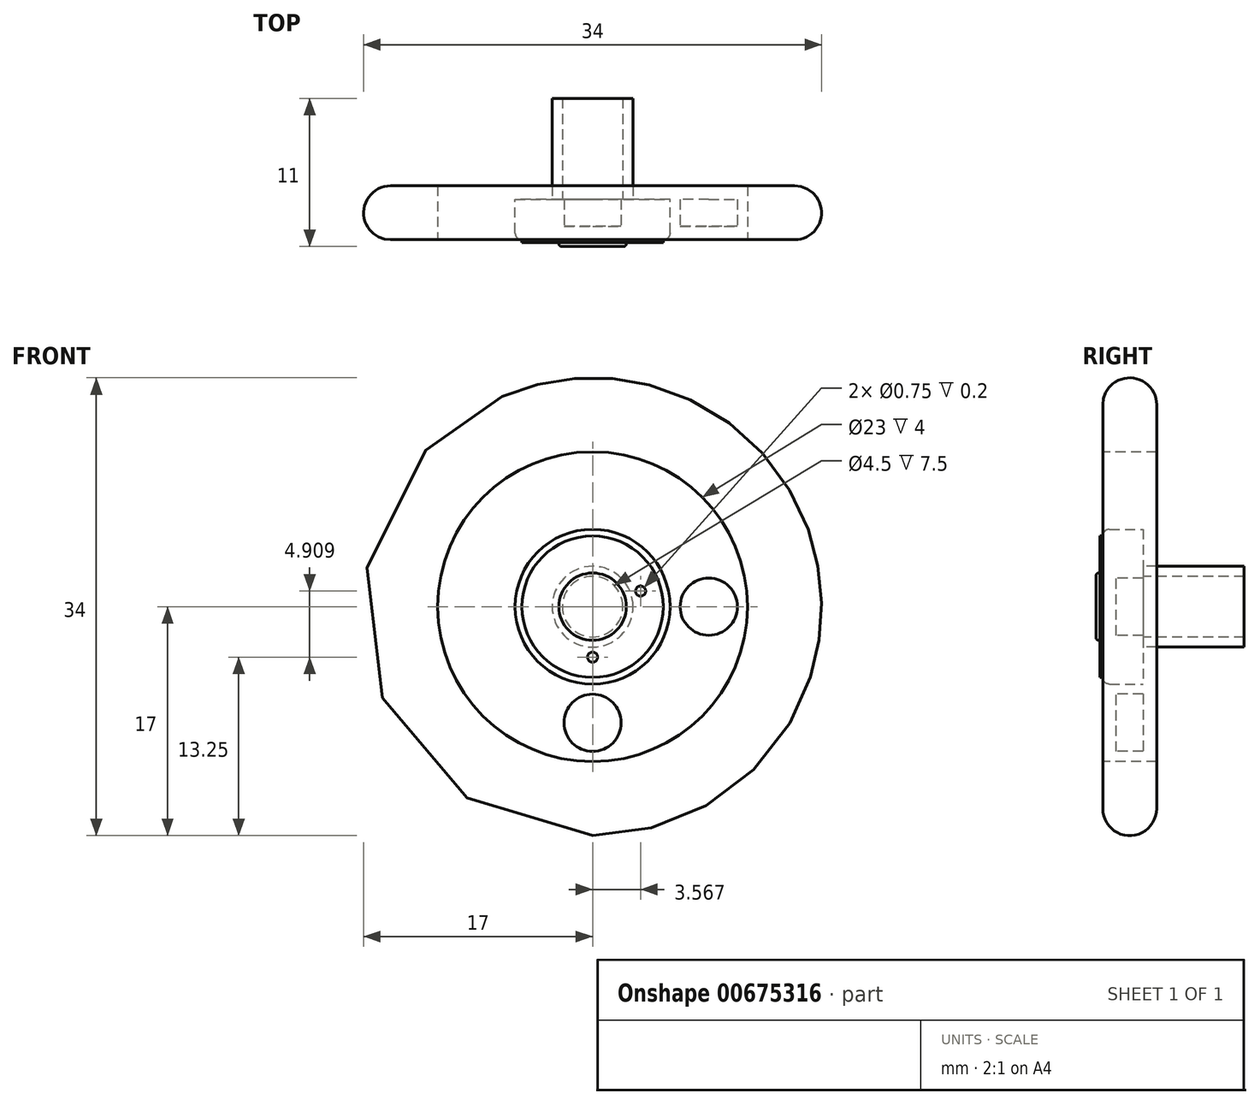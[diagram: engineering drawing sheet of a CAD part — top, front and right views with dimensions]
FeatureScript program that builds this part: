
annotation { "Feature Type Name" : "Feature", "Feature Type Description" : "" }
export const myFeature = defineFeature(function(context is Context, id is Id, definition is map)
    precondition{}
    {
        {
            var Q0;
            Q0=qCreatedBy(makeId("Front.planeOp"),FACE);
            var sketch = newSketch(context, id + "F0", { "sketchPlane" : qUnion([Q0])});
            skCircle(sketch, "E0", {"center": v(0, 0) * mm, "radius": 17 * mm});
            skSolve(sketch);
        }
        {
            var Q0;
            Q0 = qSketchRegion(id + "F0", true);
            extrude(context, id + "F1", {"entities" : qUnion([Q0]), "oppositeDirection" : true, "depth" : 4 * mm, "offsetDistance" : 25.4 * mm});
        }
        {
            var Q0;
            Q0=makeQuery(id+"F1.opExtrude","CAP_FACE",FACE,{"disambiguationData":[OSD([sQuery(id+"F0.wireOp",EDGE,"E0")])],"isStart":true});
            var sketch = newSketch(context, id + "F2", { "sketchPlane" : qUnion([Q0])});
            skCircle(sketch, "E1", {"center": v(0, 0) * mm, "radius": 11.5 * mm});
            skSolve(sketch);
        }
        {
            var Q0;
            Q0 = qSketchRegion(id + "F2", true);
            extrude(context, id + "F3", {"entities" : qUnion([Q0]), "operationType" : NewBodyOperationType.REMOVE, "oppositeDirection" : true, "depth" : 1 * mm, "offsetDistance" : 25.4 * mm});
        }
        {
            var Q0;
            Q0=makeQuery(id+"F1.opExtrude","CAP_FACE",FACE,{"disambiguationData":[OSD([sQuery(id+"F0.wireOp",EDGE,"E0")])],"isStart":false});
            var sketch = newSketch(context, id + "F4", { "sketchPlane" : qUnion([Q0])});
            skCircle(sketch, "E2", {"center": v(0, 0) * mm, "radius": 11.5 * mm});
            skSolve(sketch);
        }
        {
            var Q0;
            Q0 = qSketchRegion(id + "F4", true);
            extrude(context, id + "F5", {"entities" : qUnion([Q0]), "operationType" : NewBodyOperationType.REMOVE, "oppositeDirection" : true, "depth" : 1 * mm, "offsetDistance" : 25.4 * mm});
        }
        {
            var Q0;
            Q0=makeQuery(id+"F1.opExtrude","CAP_EDGE",EDGE,{"disambiguationData":[OSD([sQuery(id+"F0.wireOp",EDGE,"E0")])],"isStart":true});
            fillet(context, id + "F6", {"entities" : qUnion([Q0]), "radius" : 2 * mm, "tangentPropagation" : true, "allowEdgeOverflow" : false});
        }
        {
            var Q0;
            Q0=makeQuery(id+"F1.opExtrude","CAP_EDGE",EDGE,{"disambiguationData":[OSD([sQuery(id+"F0.wireOp",EDGE,"E0")])],"isStart":false});
            fillet(context, id + "F7", {"entities" : qUnion([Q0]), "radius" : 2 * mm, "tangentPropagation" : true, "allowEdgeOverflow" : false});
        }
        {
            var Q0;
            Q0=makeQuery(id+"F3.boolean.opBoolean","COPY",FACE,{"derivedFrom":makeQuery(id+"F3.opExtrude","CAP_FACE",FACE,{"disambiguationData":[OSD([sQuery(id+"F2.wireOp",EDGE,"E1")])],"isStart":false})});
            var sketch = newSketch(context, id + "F8", { "sketchPlane" : qUnion([Q0])});
            skCircle(sketch, "E3", {"center": v(0, 0) * mm, "radius": 2.5 * mm});
            skSolve(sketch);
        }
        {
            var Q0;
            Q0 = qSketchRegion(id + "F8", true);
            extrude(context, id + "F9", {"entities" : qUnion([Q0]), "operationType" : NewBodyOperationType.ADD, "depth" : 1.5 * mm, "offsetDistance" : 25.4 * mm});
        }
        {
            var Q0;
            Q0=makeQuery(id+"F3.boolean.opBoolean","COPY",FACE,{"derivedFrom":makeQuery(id+"F3.opExtrude","CAP_FACE",FACE,{"disambiguationData":[OSD([sQuery(id+"F2.wireOp",EDGE,"E1")])],"isStart":false})});
            var sketch = newSketch(context, id + "F10", { "sketchPlane" : qUnion([Q0])});
            skCircle(sketch, "E4", {"center": v(0, 0) * mm, "radius": 5.75 * mm});
            skSolve(sketch);
        }
        {
            var Q0;
            Q0 = qSketchRegion(id + "F10", true);
            extrude(context, id + "F11", {"entities" : qUnion([Q0]), "operationType" : NewBodyOperationType.ADD, "depth" : 1 * mm, "offsetDistance" : 25.4 * mm});
        }
        {
            var Q0;
            Q0=makeQuery(id+"F11.opExtrude","CAP_EDGE",EDGE,{"disambiguationData":[OSD([sQuery(id+"F10.wireOp",EDGE,"E4")])],"isStart":false});
            fillet(context, id + "F12", {"entities" : qUnion([Q0]), "radius" : .5 * mm, "tangentPropagation" : true, "allowEdgeOverflow" : false});
        }
        {
            var Q0;
            Q0=makeQuery(id+"F9.opExtrude","CAP_EDGE",EDGE,{"disambiguationData":[OSD([sQuery(id+"F8.wireOp",EDGE,"E3")])],"isStart":false});
            fillet(context, id + "F13", {"entities" : qUnion([Q0]), "radius" : .2 * mm, "tangentPropagation" : true, "allowEdgeOverflow" : false});
        }
        {
            var Q0;
            Q0=makeQuery(id+"F3.boolean.opBoolean","COPY",FACE,{"derivedFrom":makeQuery(id+"F3.opExtrude","CAP_FACE",FACE,{"disambiguationData":[OSD([sQuery(id+"F2.wireOp",EDGE,"E1")])],"isStart":false})});
            var sketch = newSketch(context, id + "F14", { "sketchPlane" : qUnion([Q0])});
            skCircle(sketch, "E5", {"center": v(0, 0) * mm, "radius": 8.62 * mm});
            skCircle(sketch, "E6", {"center": v(0, 8.62) * mm, "radius": 2.12 * mm});
            skCircle(sketch, "E7.1.0", {"center": v(-6.1, 6.1) * mm, "radius": 2.12 * mm});
            skCircle(sketch, "E7.2.0", {"center": v(-8.62, 0) * mm, "radius": 2.12 * mm});
            skCircle(sketch, "E7.3.0", {"center": v(-6.1, -6.1) * mm, "radius": 2.12 * mm});
            skCircle(sketch, "E7.4.0", {"center": v(0, -8.62) * mm, "radius": 2.12 * mm});
            skCircle(sketch, "E7.5.0", {"center": v(6.1, -6.1) * mm, "radius": 2.12 * mm});
            skCircle(sketch, "E7.6.0", {"center": v(8.62, 0) * mm, "radius": 2.12 * mm});
            skCircle(sketch, "E7.7.0", {"center": v(6.1, 6.1) * mm, "radius": 2.12 * mm});
            skSolve(sketch);
        }
        {
            var Q0;
            {var subQ0=sQuery(id+"F14.wireOp",EDGE,"E6");var subQ1=sQuery(id+"F14.wireOp",EDGE,"E5");var subQ2=makeQuery(id+"F14.imprint","INTERSECT",VERTEX,{"disambiguationData":[OD(0.0)],"derivedFrom":[subQ1,subQ0]});Q0=makeQuery(id+"F14.imprint","IMPRINT",FACE,{"disambiguationData":[TD([[makeQuery(id+"F14.imprint","IMPRINT",EDGE,{"disambiguationData":[TD([[subQ2,-1.0]])],"derivedFrom":subQ1}),1.0]])]});}
            var Q1;
            {var subQ0=sQuery(id+"F14.wireOp",EDGE,"E6");var subQ1=sQuery(id+"F14.wireOp",EDGE,"E5");var subQ2=makeQuery(id+"F14.imprint","INTERSECT",VERTEX,{"disambiguationData":[OD(0.0)],"derivedFrom":[subQ1,subQ0]});Q1=makeQuery(id+"F14.imprint","IMPRINT",FACE,{"disambiguationData":[TD([[makeQuery(id+"F14.imprint","IMPRINT",EDGE,{"disambiguationData":[TD([[subQ2,-1.0]])],"derivedFrom":subQ1}),-1.0]])]});}
            var Q2;
            {var subQ0=sQuery(id+"F14.wireOp",EDGE,"E7.1.0");var subQ1=sQuery(id+"F14.wireOp",EDGE,"E5");var subQ2=makeQuery(id+"F14.imprint","INTERSECT",VERTEX,{"disambiguationData":[OD(0.0)],"derivedFrom":[subQ1,subQ0]});Q2=makeQuery(id+"F14.imprint","IMPRINT",FACE,{"disambiguationData":[TD([[makeQuery(id+"F14.imprint","IMPRINT",EDGE,{"disambiguationData":[TD([[subQ2,-1.0]])],"derivedFrom":subQ1}),1.0]])]});}
            var Q3;
            {var subQ0=sQuery(id+"F14.wireOp",EDGE,"E7.1.0");var subQ1=sQuery(id+"F14.wireOp",EDGE,"E5");var subQ2=makeQuery(id+"F14.imprint","INTERSECT",VERTEX,{"disambiguationData":[OD(0.0)],"derivedFrom":[subQ1,subQ0]});Q3=makeQuery(id+"F14.imprint","IMPRINT",FACE,{"disambiguationData":[TD([[makeQuery(id+"F14.imprint","IMPRINT",EDGE,{"disambiguationData":[TD([[subQ2,-1.0]])],"derivedFrom":subQ1}),-1.0]])]});}
            var Q4;
            {var subQ0=sQuery(id+"F14.wireOp",EDGE,"E7.2.0");var subQ1=sQuery(id+"F14.wireOp",EDGE,"E5");var subQ2=makeQuery(id+"F14.imprint","INTERSECT",VERTEX,{"disambiguationData":[OD(0.0)],"derivedFrom":[subQ1,subQ0]});Q4=makeQuery(id+"F14.imprint","IMPRINT",FACE,{"disambiguationData":[TD([[makeQuery(id+"F14.imprint","IMPRINT",EDGE,{"disambiguationData":[TD([[subQ2,-1.0]])],"derivedFrom":subQ1}),1.0]])]});}
            var Q5;
            {var subQ0=sQuery(id+"F14.wireOp",EDGE,"E7.2.0");var subQ1=sQuery(id+"F14.wireOp",EDGE,"E5");var subQ2=makeQuery(id+"F14.imprint","INTERSECT",VERTEX,{"disambiguationData":[OD(0.0)],"derivedFrom":[subQ1,subQ0]});Q5=makeQuery(id+"F14.imprint","IMPRINT",FACE,{"disambiguationData":[TD([[makeQuery(id+"F14.imprint","IMPRINT",EDGE,{"disambiguationData":[TD([[subQ2,-1.0]])],"derivedFrom":subQ1}),-1.0]])]});}
            var Q6;
            {var subQ0=sQuery(id+"F14.wireOp",EDGE,"E7.3.0");var subQ1=sQuery(id+"F14.wireOp",EDGE,"E5");var subQ2=makeQuery(id+"F14.imprint","INTERSECT",VERTEX,{"disambiguationData":[OD(0.0)],"derivedFrom":[subQ1,subQ0]});Q6=makeQuery(id+"F14.imprint","IMPRINT",FACE,{"disambiguationData":[TD([[makeQuery(id+"F14.imprint","IMPRINT",EDGE,{"disambiguationData":[TD([[subQ2,-1.0]])],"derivedFrom":subQ1}),-1.0]])]});}
            var Q7;
            {var subQ0=sQuery(id+"F14.wireOp",EDGE,"E7.3.0");var subQ1=sQuery(id+"F14.wireOp",EDGE,"E5");var subQ2=makeQuery(id+"F14.imprint","INTERSECT",VERTEX,{"disambiguationData":[OD(0.0)],"derivedFrom":[subQ1,subQ0]});Q7=makeQuery(id+"F14.imprint","IMPRINT",FACE,{"disambiguationData":[TD([[makeQuery(id+"F14.imprint","IMPRINT",EDGE,{"disambiguationData":[TD([[subQ2,-1.0]])],"derivedFrom":subQ1}),1.0]])]});}
            var Q8;
            {var subQ0=sQuery(id+"F14.wireOp",EDGE,"E7.4.0");var subQ1=sQuery(id+"F14.wireOp",EDGE,"E5");var subQ2=makeQuery(id+"F14.imprint","INTERSECT",VERTEX,{"disambiguationData":[OD(0.0)],"derivedFrom":[subQ1,subQ0]});Q8=makeQuery(id+"F14.imprint","IMPRINT",FACE,{"disambiguationData":[TD([[makeQuery(id+"F14.imprint","IMPRINT",EDGE,{"disambiguationData":[TD([[subQ2,-1.0]])],"derivedFrom":subQ1}),-1.0]])]});}
            var Q9;
            {var subQ0=sQuery(id+"F14.wireOp",EDGE,"E7.4.0");var subQ1=sQuery(id+"F14.wireOp",EDGE,"E5");var subQ2=makeQuery(id+"F14.imprint","INTERSECT",VERTEX,{"disambiguationData":[OD(0.0)],"derivedFrom":[subQ1,subQ0]});Q9=makeQuery(id+"F14.imprint","IMPRINT",FACE,{"disambiguationData":[TD([[makeQuery(id+"F14.imprint","IMPRINT",EDGE,{"disambiguationData":[TD([[subQ2,-1.0]])],"derivedFrom":subQ1}),1.0]])]});}
            var Q10;
            {var subQ0=sQuery(id+"F14.wireOp",EDGE,"E7.5.0");var subQ1=sQuery(id+"F14.wireOp",EDGE,"E5");var subQ2=makeQuery(id+"F14.imprint","INTERSECT",VERTEX,{"disambiguationData":[OD(0.0)],"derivedFrom":[subQ1,subQ0]});Q10=makeQuery(id+"F14.imprint","IMPRINT",FACE,{"disambiguationData":[TD([[makeQuery(id+"F14.imprint","IMPRINT",EDGE,{"disambiguationData":[TD([[subQ2,-1.0]])],"derivedFrom":subQ1}),-1.0]])]});}
            var Q11;
            {var subQ0=sQuery(id+"F14.wireOp",EDGE,"E7.5.0");var subQ1=sQuery(id+"F14.wireOp",EDGE,"E5");var subQ2=makeQuery(id+"F14.imprint","INTERSECT",VERTEX,{"disambiguationData":[OD(0.0)],"derivedFrom":[subQ1,subQ0]});Q11=makeQuery(id+"F14.imprint","IMPRINT",FACE,{"disambiguationData":[TD([[makeQuery(id+"F14.imprint","IMPRINT",EDGE,{"disambiguationData":[TD([[subQ2,-1.0]])],"derivedFrom":subQ1}),1.0]])]});}
            var Q12;
            {var subQ0=sQuery(id+"F14.wireOp",EDGE,"E7.6.0");var subQ1=sQuery(id+"F14.wireOp",EDGE,"E5");var subQ2=makeQuery(id+"F14.imprint","INTERSECT",VERTEX,{"disambiguationData":[OD(0.0)],"derivedFrom":[subQ1,subQ0]});Q12=makeQuery(id+"F14.imprint","IMPRINT",FACE,{"disambiguationData":[TD([[makeQuery(id+"F14.imprint","IMPRINT",EDGE,{"disambiguationData":[TD([[subQ2,1.0]])],"derivedFrom":subQ1}),1.0]])]});}
            var Q13;
            {var subQ0=sQuery(id+"F14.wireOp",EDGE,"E7.6.0");var subQ1=sQuery(id+"F14.wireOp",EDGE,"E5");var subQ2=makeQuery(id+"F14.imprint","INTERSECT",VERTEX,{"disambiguationData":[OD(0.0)],"derivedFrom":[subQ1,subQ0]});Q13=makeQuery(id+"F14.imprint","IMPRINT",FACE,{"disambiguationData":[TD([[makeQuery(id+"F14.imprint","IMPRINT",EDGE,{"disambiguationData":[TD([[subQ2,1.0]])],"derivedFrom":subQ1}),-1.0]])]});}
            var Q14;
            {var subQ0=sQuery(id+"F14.wireOp",EDGE,"E7.7.0");var subQ1=sQuery(id+"F14.wireOp",EDGE,"E5");var subQ2=makeQuery(id+"F14.imprint","INTERSECT",VERTEX,{"disambiguationData":[OD(0.0)],"derivedFrom":[subQ1,subQ0]});Q14=makeQuery(id+"F14.imprint","IMPRINT",FACE,{"disambiguationData":[TD([[makeQuery(id+"F14.imprint","IMPRINT",EDGE,{"disambiguationData":[TD([[subQ2,-1.0]])],"derivedFrom":subQ1}),-1.0]])]});}
            var Q15;
            {var subQ0=sQuery(id+"F14.wireOp",EDGE,"E7.7.0");var subQ1=sQuery(id+"F14.wireOp",EDGE,"E5");var subQ2=makeQuery(id+"F14.imprint","INTERSECT",VERTEX,{"disambiguationData":[OD(0.0)],"derivedFrom":[subQ1,subQ0]});Q15=makeQuery(id+"F14.imprint","IMPRINT",FACE,{"disambiguationData":[TD([[makeQuery(id+"F14.imprint","IMPRINT",EDGE,{"disambiguationData":[TD([[subQ2,-1.0]])],"derivedFrom":subQ1}),1.0]])]});}
            extrude(context, id + "F15", {"entities" : qUnion([Q0, Q1, Q2, Q3, Q4, Q5, Q6, Q7, Q8, Q9, Q10, Q11, Q12, Q13, Q14, Q15]), "operationType" : NewBodyOperationType.REMOVE, "oppositeDirection" : true, "depth" : 25.4 * mm, "offsetDistance" : 25.4 * mm});
        }
        {
            var Q0;
            Q0=makeQuery(id+"F5.boolean.opBoolean","COPY",FACE,{"derivedFrom":makeQuery(id+"F5.opExtrude","CAP_FACE",FACE,{"disambiguationData":[OSD([sQuery(id+"F4.wireOp",EDGE,"E2")])],"isStart":false})});
            var sketch = newSketch(context, id + "F16", { "sketchPlane" : qUnion([Q0])});
            skCircle(sketch, "E8", {"center": v(0, 0) * mm, "radius": 2.25 * mm});
            skCircle(sketch, "E9", {"center": v(0, 0) * mm, "radius": 3 * mm});
            skSolve(sketch);
        }
        {
            var Q0;
            Q0 = qSketchRegion(id + "F16", true);
            extrude(context, id + "F17", {"entities" : qUnion([Q0]), "operationType" : NewBodyOperationType.ADD, "depth" : 7.5 * mm, "offsetDistance" : 25.4 * mm});
        }
        {
            var Q0;
            Q0=makeQuery(id+"F11.opExtrude","CAP_FACE",FACE,{"disambiguationData":[OSD([sQuery(id+"F10.wireOp",EDGE,"E4")])],"isStart":false});
            var sketch = newSketch(context, id + "F18", { "sketchPlane" : qUnion([Q0])});
            skCircle(sketch, "E10", {"center": v(0, 0) * mm, "radius": 3.75 * mm});
            skCircle(sketch, "E11", {"center": v(0, 3.75) * mm, "radius": 0.38 * mm});
            skCircle(sketch, "E12.1.0", {"center": v(-2.2, 3.03) * mm, "radius": 0.38 * mm});
            skCircle(sketch, "E12.2.0", {"center": v(-3.57, 1.16) * mm, "radius": 0.38 * mm});
            skCircle(sketch, "E12.3.0", {"center": v(-3.57, -1.16) * mm, "radius": 0.38 * mm});
            skCircle(sketch, "E12.4.0", {"center": v(-2.2, -3.03) * mm, "radius": 0.38 * mm});
            skCircle(sketch, "E12.5.0", {"center": v(0, -3.75) * mm, "radius": 0.38 * mm});
            skCircle(sketch, "E12.6.0", {"center": v(2.2, -3.03) * mm, "radius": 0.38 * mm});
            skCircle(sketch, "E12.7.0", {"center": v(3.57, -1.16) * mm, "radius": 0.38 * mm});
            skCircle(sketch, "E12.8.0", {"center": v(3.57, 1.16) * mm, "radius": 0.38 * mm});
            skCircle(sketch, "E12.9.0", {"center": v(2.2, 3.03) * mm, "radius": 0.38 * mm});
            skSolve(sketch);
        }
        {
            var Q0;
            {var subQ0=sQuery(id+"F18.wireOp",EDGE,"E12.1.0");var subQ1=sQuery(id+"F18.wireOp",EDGE,"E10");var subQ2=makeQuery(id+"F18.imprint","INTERSECT",VERTEX,{"disambiguationData":[OD(0.0)],"derivedFrom":[subQ1,subQ0]});Q0=makeQuery(id+"F18.imprint","IMPRINT",FACE,{"disambiguationData":[TD([[makeQuery(id+"F18.imprint","IMPRINT",EDGE,{"disambiguationData":[TD([[subQ2,-1.0]])],"derivedFrom":subQ1}),1.0]])]});}
            var Q1;
            {var subQ0=sQuery(id+"F18.wireOp",EDGE,"E12.1.0");var subQ1=sQuery(id+"F18.wireOp",EDGE,"E10");var subQ2=makeQuery(id+"F18.imprint","INTERSECT",VERTEX,{"disambiguationData":[OD(0.0)],"derivedFrom":[subQ1,subQ0]});Q1=makeQuery(id+"F18.imprint","IMPRINT",FACE,{"disambiguationData":[TD([[makeQuery(id+"F18.imprint","IMPRINT",EDGE,{"disambiguationData":[TD([[subQ2,-1.0]])],"derivedFrom":subQ1}),-1.0]])]});}
            var Q2;
            {var subQ0=sQuery(id+"F18.wireOp",EDGE,"E11");var subQ1=sQuery(id+"F18.wireOp",EDGE,"E10");var subQ2=makeQuery(id+"F18.imprint","INTERSECT",VERTEX,{"disambiguationData":[OD(0.0)],"derivedFrom":[subQ1,subQ0]});Q2=makeQuery(id+"F18.imprint","IMPRINT",FACE,{"disambiguationData":[TD([[makeQuery(id+"F18.imprint","IMPRINT",EDGE,{"disambiguationData":[TD([[subQ2,-1.0]])],"derivedFrom":subQ1}),1.0]])]});}
            var Q3;
            {var subQ0=sQuery(id+"F18.wireOp",EDGE,"E11");var subQ1=sQuery(id+"F18.wireOp",EDGE,"E10");var subQ2=makeQuery(id+"F18.imprint","INTERSECT",VERTEX,{"disambiguationData":[OD(0.0)],"derivedFrom":[subQ1,subQ0]});Q3=makeQuery(id+"F18.imprint","IMPRINT",FACE,{"disambiguationData":[TD([[makeQuery(id+"F18.imprint","IMPRINT",EDGE,{"disambiguationData":[TD([[subQ2,-1.0]])],"derivedFrom":subQ1}),-1.0]])]});}
            var Q4;
            {var subQ0=sQuery(id+"F18.wireOp",EDGE,"E12.9.0");var subQ1=sQuery(id+"F18.wireOp",EDGE,"E10");var subQ2=makeQuery(id+"F18.imprint","INTERSECT",VERTEX,{"disambiguationData":[OD(0.0)],"derivedFrom":[subQ1,subQ0]});Q4=makeQuery(id+"F18.imprint","IMPRINT",FACE,{"disambiguationData":[TD([[makeQuery(id+"F18.imprint","IMPRINT",EDGE,{"disambiguationData":[TD([[subQ2,-1.0]])],"derivedFrom":subQ1}),1.0]])]});}
            var Q5;
            {var subQ0=sQuery(id+"F18.wireOp",EDGE,"E12.9.0");var subQ1=sQuery(id+"F18.wireOp",EDGE,"E10");var subQ2=makeQuery(id+"F18.imprint","INTERSECT",VERTEX,{"disambiguationData":[OD(0.0)],"derivedFrom":[subQ1,subQ0]});Q5=makeQuery(id+"F18.imprint","IMPRINT",FACE,{"disambiguationData":[TD([[makeQuery(id+"F18.imprint","IMPRINT",EDGE,{"disambiguationData":[TD([[subQ2,-1.0]])],"derivedFrom":subQ1}),-1.0]])]});}
            var Q6;
            {var subQ0=sQuery(id+"F18.wireOp",EDGE,"E12.8.0");var subQ1=sQuery(id+"F18.wireOp",EDGE,"E10");var subQ2=makeQuery(id+"F18.imprint","INTERSECT",VERTEX,{"disambiguationData":[OD(0.0)],"derivedFrom":[subQ1,subQ0]});Q6=makeQuery(id+"F18.imprint","IMPRINT",FACE,{"disambiguationData":[TD([[makeQuery(id+"F18.imprint","IMPRINT",EDGE,{"disambiguationData":[TD([[subQ2,1.0]])],"derivedFrom":subQ1}),1.0]])]});}
            var Q7;
            {var subQ0=sQuery(id+"F18.wireOp",EDGE,"E12.8.0");var subQ1=sQuery(id+"F18.wireOp",EDGE,"E10");var subQ2=makeQuery(id+"F18.imprint","INTERSECT",VERTEX,{"disambiguationData":[OD(0.0)],"derivedFrom":[subQ1,subQ0]});Q7=makeQuery(id+"F18.imprint","IMPRINT",FACE,{"disambiguationData":[TD([[makeQuery(id+"F18.imprint","IMPRINT",EDGE,{"disambiguationData":[TD([[subQ2,1.0]])],"derivedFrom":subQ1}),-1.0]])]});}
            var Q8;
            {var subQ0=sQuery(id+"F18.wireOp",EDGE,"E12.7.0");var subQ1=sQuery(id+"F18.wireOp",EDGE,"E10");var subQ2=makeQuery(id+"F18.imprint","INTERSECT",VERTEX,{"disambiguationData":[OD(0.0)],"derivedFrom":[subQ1,subQ0]});Q8=makeQuery(id+"F18.imprint","IMPRINT",FACE,{"disambiguationData":[TD([[makeQuery(id+"F18.imprint","IMPRINT",EDGE,{"disambiguationData":[TD([[subQ2,-1.0]])],"derivedFrom":subQ1}),1.0]])]});}
            var Q9;
            {var subQ0=sQuery(id+"F18.wireOp",EDGE,"E12.7.0");var subQ1=sQuery(id+"F18.wireOp",EDGE,"E10");var subQ2=makeQuery(id+"F18.imprint","INTERSECT",VERTEX,{"disambiguationData":[OD(0.0)],"derivedFrom":[subQ1,subQ0]});Q9=makeQuery(id+"F18.imprint","IMPRINT",FACE,{"disambiguationData":[TD([[makeQuery(id+"F18.imprint","IMPRINT",EDGE,{"disambiguationData":[TD([[subQ2,-1.0]])],"derivedFrom":subQ1}),-1.0]])]});}
            var Q10;
            {var subQ0=sQuery(id+"F18.wireOp",EDGE,"E12.6.0");var subQ1=sQuery(id+"F18.wireOp",EDGE,"E10");var subQ2=makeQuery(id+"F18.imprint","INTERSECT",VERTEX,{"disambiguationData":[OD(0.0)],"derivedFrom":[subQ1,subQ0]});Q10=makeQuery(id+"F18.imprint","IMPRINT",FACE,{"disambiguationData":[TD([[makeQuery(id+"F18.imprint","IMPRINT",EDGE,{"disambiguationData":[TD([[subQ2,-1.0]])],"derivedFrom":subQ1}),-1.0]])]});}
            var Q11;
            {var subQ0=sQuery(id+"F18.wireOp",EDGE,"E12.6.0");var subQ1=sQuery(id+"F18.wireOp",EDGE,"E10");var subQ2=makeQuery(id+"F18.imprint","INTERSECT",VERTEX,{"disambiguationData":[OD(0.0)],"derivedFrom":[subQ1,subQ0]});Q11=makeQuery(id+"F18.imprint","IMPRINT",FACE,{"disambiguationData":[TD([[makeQuery(id+"F18.imprint","IMPRINT",EDGE,{"disambiguationData":[TD([[subQ2,-1.0]])],"derivedFrom":subQ1}),1.0]])]});}
            var Q12;
            {var subQ0=sQuery(id+"F18.wireOp",EDGE,"E12.5.0");var subQ1=sQuery(id+"F18.wireOp",EDGE,"E10");var subQ2=makeQuery(id+"F18.imprint","INTERSECT",VERTEX,{"disambiguationData":[OD(0.0)],"derivedFrom":[subQ1,subQ0]});Q12=makeQuery(id+"F18.imprint","IMPRINT",FACE,{"disambiguationData":[TD([[makeQuery(id+"F18.imprint","IMPRINT",EDGE,{"disambiguationData":[TD([[subQ2,-1.0]])],"derivedFrom":subQ1}),-1.0]])]});}
            var Q13;
            {var subQ0=sQuery(id+"F18.wireOp",EDGE,"E12.5.0");var subQ1=sQuery(id+"F18.wireOp",EDGE,"E10");var subQ2=makeQuery(id+"F18.imprint","INTERSECT",VERTEX,{"disambiguationData":[OD(0.0)],"derivedFrom":[subQ1,subQ0]});Q13=makeQuery(id+"F18.imprint","IMPRINT",FACE,{"disambiguationData":[TD([[makeQuery(id+"F18.imprint","IMPRINT",EDGE,{"disambiguationData":[TD([[subQ2,-1.0]])],"derivedFrom":subQ1}),1.0]])]});}
            var Q14;
            {var subQ0=sQuery(id+"F18.wireOp",EDGE,"E12.4.0");var subQ1=sQuery(id+"F18.wireOp",EDGE,"E10");var subQ2=makeQuery(id+"F18.imprint","INTERSECT",VERTEX,{"disambiguationData":[OD(0.0)],"derivedFrom":[subQ1,subQ0]});Q14=makeQuery(id+"F18.imprint","IMPRINT",FACE,{"disambiguationData":[TD([[makeQuery(id+"F18.imprint","IMPRINT",EDGE,{"disambiguationData":[TD([[subQ2,-1.0]])],"derivedFrom":subQ1}),-1.0]])]});}
            var Q15;
            {var subQ0=sQuery(id+"F18.wireOp",EDGE,"E12.4.0");var subQ1=sQuery(id+"F18.wireOp",EDGE,"E10");var subQ2=makeQuery(id+"F18.imprint","INTERSECT",VERTEX,{"disambiguationData":[OD(0.0)],"derivedFrom":[subQ1,subQ0]});Q15=makeQuery(id+"F18.imprint","IMPRINT",FACE,{"disambiguationData":[TD([[makeQuery(id+"F18.imprint","IMPRINT",EDGE,{"disambiguationData":[TD([[subQ2,-1.0]])],"derivedFrom":subQ1}),1.0]])]});}
            var Q16;
            {var subQ0=sQuery(id+"F18.wireOp",EDGE,"E12.3.0");var subQ1=sQuery(id+"F18.wireOp",EDGE,"E10");var subQ2=makeQuery(id+"F18.imprint","INTERSECT",VERTEX,{"disambiguationData":[OD(0.0)],"derivedFrom":[subQ1,subQ0]});Q16=makeQuery(id+"F18.imprint","IMPRINT",FACE,{"disambiguationData":[TD([[makeQuery(id+"F18.imprint","IMPRINT",EDGE,{"disambiguationData":[TD([[subQ2,-1.0]])],"derivedFrom":subQ1}),-1.0]])]});}
            var Q17;
            {var subQ0=sQuery(id+"F18.wireOp",EDGE,"E12.3.0");var subQ1=sQuery(id+"F18.wireOp",EDGE,"E10");var subQ2=makeQuery(id+"F18.imprint","INTERSECT",VERTEX,{"disambiguationData":[OD(0.0)],"derivedFrom":[subQ1,subQ0]});Q17=makeQuery(id+"F18.imprint","IMPRINT",FACE,{"disambiguationData":[TD([[makeQuery(id+"F18.imprint","IMPRINT",EDGE,{"disambiguationData":[TD([[subQ2,-1.0]])],"derivedFrom":subQ1}),1.0]])]});}
            var Q18;
            {var subQ0=sQuery(id+"F18.wireOp",EDGE,"E12.2.0");var subQ1=sQuery(id+"F18.wireOp",EDGE,"E10");var subQ2=makeQuery(id+"F18.imprint","INTERSECT",VERTEX,{"disambiguationData":[OD(0.0)],"derivedFrom":[subQ1,subQ0]});Q18=makeQuery(id+"F18.imprint","IMPRINT",FACE,{"disambiguationData":[TD([[makeQuery(id+"F18.imprint","IMPRINT",EDGE,{"disambiguationData":[TD([[subQ2,-1.0]])],"derivedFrom":subQ1}),-1.0]])]});}
            var Q19;
            {var subQ0=sQuery(id+"F18.wireOp",EDGE,"E12.2.0");var subQ1=sQuery(id+"F18.wireOp",EDGE,"E10");var subQ2=makeQuery(id+"F18.imprint","INTERSECT",VERTEX,{"disambiguationData":[OD(0.0)],"derivedFrom":[subQ1,subQ0]});Q19=makeQuery(id+"F18.imprint","IMPRINT",FACE,{"disambiguationData":[TD([[makeQuery(id+"F18.imprint","IMPRINT",EDGE,{"disambiguationData":[TD([[subQ2,-1.0]])],"derivedFrom":subQ1}),1.0]])]});}
            extrude(context, id + "F19", {"entities" : qUnion([Q0, Q1, Q2, Q3, Q4, Q5, Q6, Q7, Q8, Q9, Q10, Q11, Q12, Q13, Q14, Q15, Q16, Q17, Q18, Q19]), "operationType" : NewBodyOperationType.ADD, "depth" : .2 * mm, "offsetDistance" : 25.4 * mm});
        }
    });
